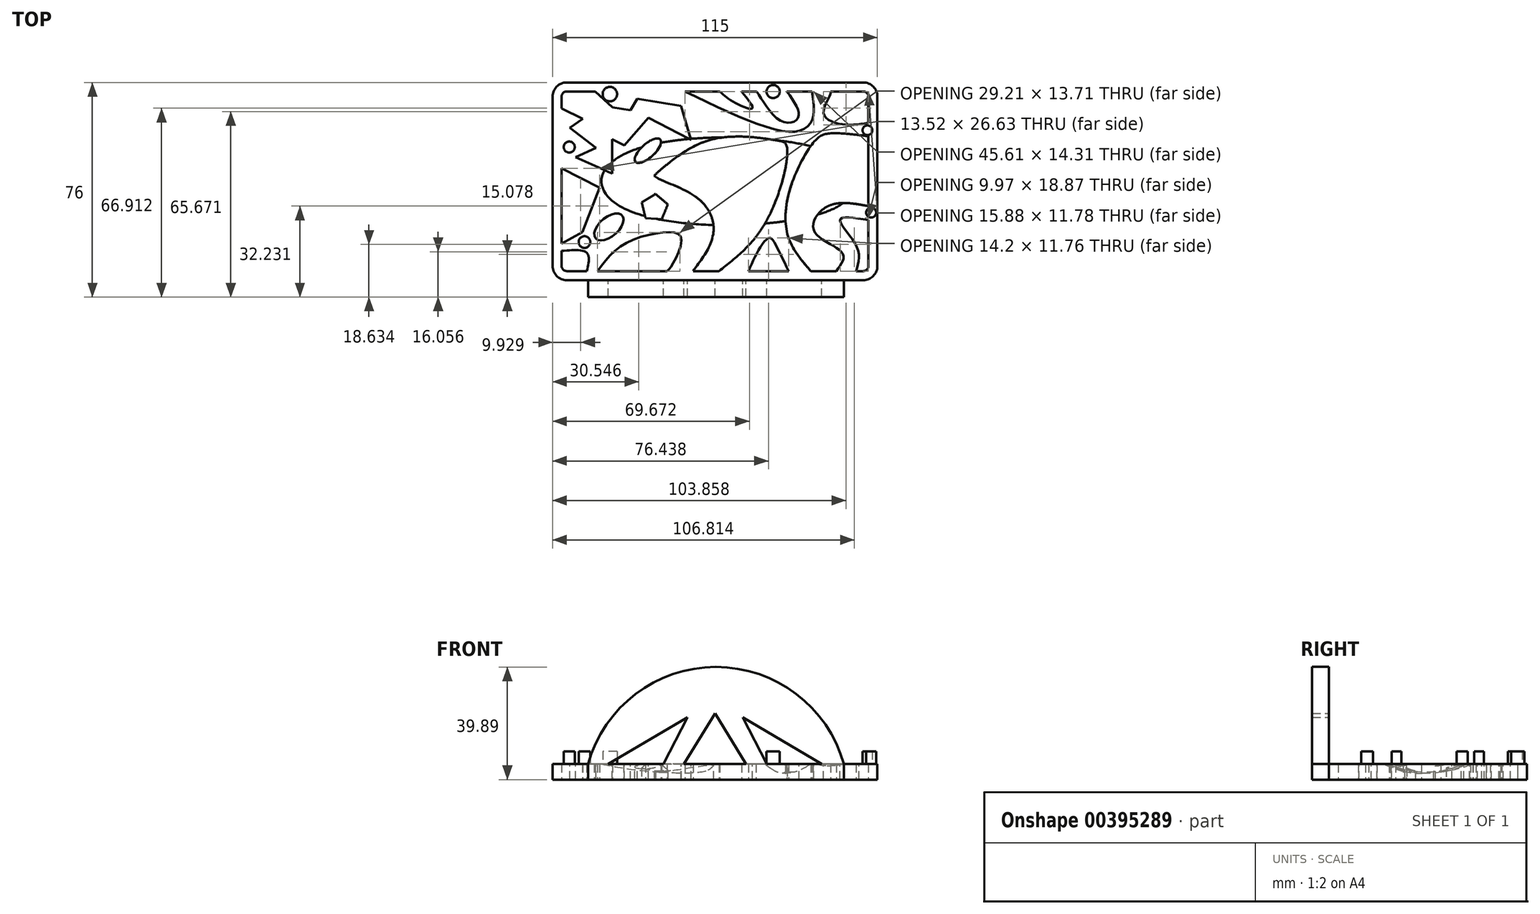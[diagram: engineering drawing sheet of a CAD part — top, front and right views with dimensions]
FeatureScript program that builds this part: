
annotation { "Feature Type Name" : "Feature", "Feature Type Description" : "" }
export const myFeature = defineFeature(function(context is Context, id is Id, definition is map)
    precondition{}
    {
        {
            var Q0;
            Q0=qCreatedBy(makeId("Top.planeOp"),FACE);
            var sketch = newSketch(context, id + "F0", { "sketchPlane" : qUnion([Q0])});
            skLineSegment(sketch, "E0.bottom", {"start": v(0, 0) * mm, "end": v(115, 0) * mm});
            skLineSegment(sketch, "E0.top", {"start": v(0, 70) * mm, "end": v(115, 70) * mm});
            skLineSegment(sketch, "E0.left", {"start": v(0, 0) * mm, "end": v(0, 70) * mm});
            skLineSegment(sketch, "E0.right", {"start": v(115, 0) * mm, "end": v(115, 70) * mm});
            skSolve(sketch);
        }
        {
            var Q0;
            Q0 = qSketchRegion(id + "F0", true);
            extrude(context, id + "F1", {"entities" : qUnion([Q0]), "depth" : 5.5 * mm});
        }
        {
            var Q0;
            Q0=makeQuery(id+"F1.opExtrude","SWEPT_EDGE",EDGE,{"disambiguationData":[OSD([sQuery(id+"F0.wireOp",EDGE,"E0.bottom"),sQuery(id+"F0.wireOp",EDGE,"E0.right")])]});
            var Q1;
            Q1=makeQuery(id+"F1.opExtrude","SWEPT_EDGE",EDGE,{"disambiguationData":[OSD([sQuery(id+"F0.wireOp",EDGE,"E0.top"),sQuery(id+"F0.wireOp",EDGE,"E0.right")])]});
            var Q2;
            Q2=makeQuery(id+"F1.opExtrude","SWEPT_EDGE",EDGE,{"disambiguationData":[OSD([sQuery(id+"F0.wireOp",EDGE,"E0.bottom"),sQuery(id+"F0.wireOp",EDGE,"E0.left")])]});
            var Q3;
            Q3=makeQuery(id+"F1.opExtrude","SWEPT_EDGE",EDGE,{"disambiguationData":[OSD([sQuery(id+"F0.wireOp",EDGE,"E0.top"),sQuery(id+"F0.wireOp",EDGE,"E0.left")])]});
            fillet(context, id + "F2", {"entities" : qUnion([Q0, Q1, Q2, Q3]), "radius" : 5 * mm, "tangentPropagation" : true, "allowEdgeOverflow" : false});
        }
        {
            var Q0;
            Q0=makeQuery(id+"F1.opExtrude","CAP_FACE",FACE,{"disambiguationData":[OSD([sQuery(id+"F0.wireOp",EDGE,"E0.bottom"),sQuery(id+"F0.wireOp",EDGE,"E0.top"),sQuery(id+"F0.wireOp",EDGE,"E0.left"),sQuery(id+"F0.wireOp",EDGE,"E0.right")])],"isStart":false});
            var sketch = newSketch(context, id + "F3", { "sketchPlane" : qUnion([Q0])});
            skArc(sketch, "E1.0", {"start": v(111.8, 65) * mm, "mid": v(111.27, 66.27) * mm, "end": v(110, 66.8) * mm});
            skLineSegment(sketch, "E1.1", {"start": v(111.8, 5) * mm, "end": v(111.8, 65) * mm});
            skLineSegment(sketch, "E1.2", {"start": v(110, 66.8) * mm, "end": v(5, 66.8) * mm});
            skArc(sketch, "E1.3", {"start": v(110, 3.2) * mm, "mid": v(111.27, 3.73) * mm, "end": v(111.8, 5) * mm});
            skArc(sketch, "E1.4", {"start": v(5, 66.8) * mm, "mid": v(3.73, 66.27) * mm, "end": v(3.2, 65) * mm});
            skLineSegment(sketch, "E1.5", {"start": v(3.2, 65) * mm, "end": v(3.2, 5) * mm});
            skArc(sketch, "E1.6", {"start": v(3.2, 5) * mm, "mid": v(3.73, 3.73) * mm, "end": v(5, 3.2) * mm});
            skLineSegment(sketch, "E1.7", {"start": v(5, 3.2) * mm, "end": v(110, 3.2) * mm});
            skSolve(sketch);
        }
        {
            var Q0;
            Q0=makeQuery(id+"F1.opExtrude","CAP_EDGE",EDGE,{"disambiguationData":[OSD([sQuery(id+"F0.wireOp",EDGE,"E0.right")])],"isStart":false});
            cPoint(context, id + "F4", {"entities" : qUnion([Q0]), "parameter" : 0.5});
        }
        {
            var Q0;
            Q0 = qCreatedBy(id + "F4" ,VERTEX);
            var Q1;
            Q1=qCreatedBy(makeId("Front.planeOp"),FACE);
            cPlane(context, id + "F5", {"entities" : qUnion([Q0, Q1]), "cplaneType" : CPlaneType.PLANE_POINT, "offset" : 25 * mm, "width" : 150 * mm, "height" : 150 * mm});
        }
        {
            var Q0;
            Q0=qCreatedBy(makeId("Top.planeOp"),FACE);
            var sketch = newSketch(context, id + "F6", { "sketchPlane" : qUnion([Q0])});
            skArc(sketch, "E2.0.0", {"start": v(3.2, 5) * mm, "mid": v(3.73, 3.73) * mm, "end": v(5, 3.2) * mm});
            skLineSegment(sketch, "E2.0.1", {"start": v(5, 3.2) * mm, "end": v(12.1, 3.2) * mm});
            skArc(sketch, "E2.0.2", {"start": v(110, 3.2) * mm, "mid": v(111.27, 3.73) * mm, "end": v(111.8, 5) * mm});
            skLineSegment(sketch, "E2.0.3", {"start": v(111.8, 5) * mm, "end": v(111.8, 21.3) * mm});
            skArc(sketch, "E2.0.4", {"start": v(111.8, 65) * mm, "mid": v(111.27, 66.27) * mm, "end": v(110, 66.8) * mm});
            skLineSegment(sketch, "E2.0.5", {"start": v(110, 66.8) * mm, "end": v(98.46, 66.8) * mm});
            skArc(sketch, "E2.0.6", {"start": v(5, 66.8) * mm, "mid": v(3.73, 66.27) * mm, "end": v(3.2, 65) * mm});
            skFitSpline(sketch, "E3", {"points": [v(111.8, 55.67) * mm, v(102.15, 55.24) * mm, v(95.98, 58.91) * mm, v(97.93, 64.83) * mm, v(98.46, 66.8) * mm], "startDerivative": vector(-29.87, -4.51) * mm, "endDerivative": vector(1.38, 11.14) * mm});
            skFitSpline(sketch, "E4", {"points": [v(111.8, 50.96) * mm, v(98.46, 52) * mm, v(93.18, 49.66) * mm, v(84.12, 32.4) * mm, v(83.54, 14.98) * mm, v(91.4, 3.2) * mm], "startDerivative": vector(-75.79, 9.38) * mm, "endDerivative": vector(46.5, -53.55) * mm});
            skFitSpline(sketch, "E5", {"points": [v(91.8, 66.8) * mm, v(92.04, 57.15) * mm, v(85.7, 52.56) * mm, v(46.87, 66.8) * mm], "startDerivative": vector(6.97, -41.3) * mm, "endDerivative": vector(-88.82, 42.95) * mm});
            skFitSpline(sketch, "E6", {"points": [v(58.9, 3.2) * mm, v(76.03, 21.56) * mm, v(82.86, 47.53) * mm, v(79.32, 49.48) * mm, v(54.72, 49.32) * mm, v(25.53, 27.54) * mm, v(3.2, 12.92) * mm], "startDerivative": vector(105.84, 82.15) * mm, "endDerivative": vector(-121.36, -67.42) * mm});
            skFitSpline(sketch, "E7", {"points": [v(83, 66.8) * mm, v(87.02, 57.68) * mm, v(80.58, 56.52) * mm, v(72.15, 66.8) * mm, v(72.02, 66.8) * mm], "startDerivative": vector(22.7, -31.9) * mm, "endDerivative": vector(-2.7, -1.87) * mm});
            skFitSpline(sketch, "E8", {"points": [v(66.9, 66.8) * mm, v(70.67, 60.83) * mm, v(64.36, 62.9) * mm, v(59.21, 66.8) * mm], "startDerivative": vector(19.38, -23.5) * mm, "endDerivative": vector(-12.93, 11.89) * mm});
            skFitSpline(sketch, "E9", {"points": [v(100.4, 3.2) * mm, v(102.64, 9.53) * mm, v(92.64, 17.27) * mm, v(97.1, 25.99) * mm, v(111.8, 26.2) * mm], "startDerivative": vector(25.53, 33.88) * mm, "endDerivative": vector(54.26, -10.38) * mm});
            skFitSpline(sketch, "E10", {"points": [v(83.54, 3.2) * mm, v(78.74, 12.92) * mm, v(76.9, 14.98) * mm, v(73.45, 11.57) * mm, v(69.34, 3.2) * mm], "startDerivative": vector(-16.54, 34.13) * mm, "endDerivative": vector(-12.58, -29.43) * mm});
            skFitSpline(sketch, "E11", {"points": [v(37.11, 66.8) * mm, v(56.97, 56.94) * mm, v(51.48, 53.5) * mm, v(27.34, 54.05) * mm, v(18.95, 40.98) * mm, v(3.2, 44.12) * mm], "startDerivative": vector(123.14, -43.65) * mm, "endDerivative": vector(-93.2, 43.1) * mm});
            skFitSpline(sketch, "E12", {"points": [v(49.73, 3.2) * mm, v(56.9, 16.67) * mm, v(52, 28.48) * mm, v(38.58, 35.4) * mm, v(35.9, 36.97) * mm], "startDerivative": vector(33.19, 44.6) * mm, "endDerivative": vector(-14.67, 10.37) * mm});
            skFitSpline(sketch, "E13", {"points": [v(15.94, 3.2) * mm, v(25.57, 12.92) * mm, v(41.21, 16.94) * mm, v(45.54, 14.98) * mm, v(42.48, 5.61) * mm, v(40.54, 3.2) * mm], "startDerivative": vector(31.9, 43.47) * mm, "endDerivative": vector(-14.4, -13.89) * mm});
            skLineSegment(sketch, "E14.trimOffspring", {"start": v(111.8, 55.67) * mm, "end": v(111.8, 65) * mm});
            skLineSegment(sketch, "E15.trimOffspring", {"start": v(91.8, 66.8) * mm, "end": v(83, 66.8) * mm});
            skLineSegment(sketch, "E16.trimOffspring", {"start": v(91.4, 3.2) * mm, "end": v(100.4, 3.2) * mm});
            skLineSegment(sketch, "E17.trimOffspring", {"start": v(69.34, 3.2) * mm, "end": v(83.54, 3.2) * mm});
            skLineSegment(sketch, "E18.trimOffspring", {"start": v(15.06, 66.8) * mm, "end": v(5, 66.8) * mm});
            skLineSegment(sketch, "E19.trimOffspring", {"start": v(3.2, 10.36) * mm, "end": v(3.2, 5) * mm});
            skLineSegment(sketch, "E20.trimOffspring", {"start": v(49.73, 3.2) * mm, "end": v(58.9, 3.2) * mm});
            skFitSpline(sketch, "E21", {"points": [v(12.1, 3.2) * mm, v(12.24, 9.54) * mm, v(3.2, 10.36) * mm], "startDerivative": vector(4.16, 16.75) * mm, "endDerivative": vector(-21.2, -1.88) * mm});
            skLineSegment(sketch, "E22.trimOffspring", {"start": v(72.15, 66.8) * mm, "end": v(66.9, 66.8) * mm});
            skLineSegment(sketch, "E23.trimOffspring", {"start": v(59.21, 66.8) * mm, "end": v(46.87, 66.8) * mm});
            skPoint(sketch, "E24.1.internal.orphan", {"position": v(20.32, 14.98) * mm});
            skFitSpline(sketch, "E25", {"points": [v(111.8, 21.3) * mm, v(101.78, 21.31) * mm, v(107.6, 12) * mm, v(107.5, 3.2) * mm], "startDerivative": vector(-43.28, 6.91) * mm, "endDerivative": vector(-7.66, -26.7) * mm});
            skLineSegment(sketch, "E26.trimOffspring", {"start": v(111.8, 26.2) * mm, "end": v(111.8, 50.96) * mm});
            skLineSegment(sketch, "E27.trimOffspring", {"start": v(107.5, 3.2) * mm, "end": v(110, 3.2) * mm});
            skLineSegment(sketch, "E28.trimOffspring", {"start": v(15.94, 3.2) * mm, "end": v(40.54, 3.2) * mm});
            skCircle(sketch, "E29.cCircle", {"center": v(36.07, 25.67) * mm, "radius": 3.94 * mm, "construction": true});
            skLineSegment(sketch, "E29.0", {"start": v(31.56, 27.53) * mm, "end": v(36.44, 30.53) * mm});
            skLineSegment(sketch, "E29.1", {"start": v(36.44, 30.53) * mm, "end": v(40.8, 26.81) * mm});
            skLineSegment(sketch, "E29.2", {"start": v(40.8, 26.81) * mm, "end": v(38.62, 21.52) * mm});
            skLineSegment(sketch, "E29.3", {"start": v(38.62, 21.52) * mm, "end": v(32.9, 21.96) * mm});
            skLineSegment(sketch, "E29.4", {"start": v(32.9, 21.96) * mm, "end": v(31.56, 27.53) * mm});
            skPoint(sketch, "E29.0.midPoint", {"position": v(34, 29.03) * mm});
            skEllipse(sketch, "E30", {"center": v(33.73, 45.83) * mm, "majorRadius": 5.9 * mm, "minorRadius": 2.4 * mm, "majorAxis": v(-0.74, -0.67)});
            skEllipse(sketch, "E31", {"center": v(19.93, 18.83) * mm, "majorRadius": 6.17 * mm, "minorRadius": 3.37 * mm, "majorAxis": v(-0.76, -0.65)});
            skFitSpline(sketch, "E32", {"points": [v(71.59, 14.86) * mm, v(68.14, 19.66) * mm, v(57, 18.22) * mm], "startDerivative": vector(-5.75, 14.27) * mm, "endDerivative": vector(-22.4, -6.52) * mm});
            skFitSpline(sketch, "E33", {"points": [v(77.17, 23.82) * mm, v(67.07, 25.78) * mm, v(68, 32.63) * mm, v(82.51, 40.16) * mm], "startDerivative": vector(-39.17, -0.09) * mm, "endDerivative": vector(43.07, 14.7) * mm});
            skFitSpline(sketch, "E34", {"points": [v(72.56, 50.45) * mm, v(68.9, 38.8) * mm, v(60.48, 34.86) * mm, v(59.2, 38.02) * mm, v(59.15, 50.35) * mm], "startDerivative": vector(-4.44, -43.64) * mm, "endDerivative": vector(0.5, 46.95) * mm});
            skFitSpline(sketch, "E35", {"points": [v(54.28, 26.06) * mm, v(55.75, 32.74) * mm, v(50.11, 40.64) * mm, v(41.76, 41.96) * mm], "startDerivative": vector(9.26, 20.94) * mm, "endDerivative": vector(-25.72, -0.75) * mm});
            skFitSpline(sketch, "E36.trimOffspring", {"points": [v(49.73, 3.2) * mm, v(56.9, 16.67) * mm, v(52, 28.48) * mm, v(38.58, 35.4) * mm, v(35.9, 36.97) * mm], "startDerivative": vector(33.19, 44.6) * mm, "endDerivative": vector(-14.67, 10.37) * mm});
            skLineSegment(sketch, "E37", {"start": v(83.1, 44.85) * mm, "end": v(78.59, 44.85) * mm});
            skLineSegment(sketch, "E38", {"start": v(78.59, 44.85) * mm, "end": v(77.4, 49.78) * mm});
            skLineSegment(sketch, "E39", {"start": v(3.17, 39.55) * mm, "end": v(16.69, 32.77) * mm});
            skLineSegment(sketch, "E40", {"start": v(16.69, 32.77) * mm, "end": v(10.57, 17.01) * mm});
            skLineSegment(sketch, "E41", {"start": v(3.2, 12.92) * mm, "end": v(3.17, 39.55) * mm});
            skLineSegment(sketch, "E42", {"start": v(3.2, 12.92) * mm, "end": v(10.57, 17.01) * mm});
            skLineSegment(sketch, "E43", {"start": v(28.52, 54.62) * mm, "end": v(15.06, 66.8) * mm});
            skLineSegment(sketch, "E44", {"start": v(24.23, 50.6) * mm, "end": v(3.2, 60.77) * mm});
            skLineSegment(sketch, "E45", {"start": v(3.2, 60.77) * mm, "end": v(3.2, 65) * mm});
            skLineSegment(sketch, "E46", {"start": v(97.1, 25.99) * mm, "end": v(90.65, 46.43) * mm});
            skLineSegment(sketch, "E47", {"start": v(100.7, 27.15) * mm, "end": v(102.26, 51.96) * mm});
            skSolve(sketch);
        }
        {
            var Q0;
            Q0 = qSketchRegion(id + "F6", true);
            extrude(context, id + "F7", {"entities" : qUnion([Q0]), "operationType" : NewBodyOperationType.REMOVE, "depth" : 25 * mm});
        }
        {
            var Q0;
            Q0=makeQuery(id+"F3.imprint","IMPRINT",FACE,{"disambiguationData":[TD([[makeQuery(id+"F3.imprint","IMPRINT",EDGE,{"derivedFrom":sQuery(id+"F3.wireOp",EDGE,"E1.0")}),1.0]])]});
            var sketch = newSketch(context, id + "F8", { "sketchPlane" : qUnion([Q0])});
            skLineSegment(sketch, "E48", {"start": v(48.99, 49.7) * mm, "end": v(45.5, 61.7) * mm});
            skLineSegment(sketch, "E49", {"start": v(45.5, 61.7) * mm, "end": v(30.03, 64.21) * mm});
            skLineSegment(sketch, "E50", {"start": v(30.03, 64.21) * mm, "end": v(27.51, 60.15) * mm});
            skLineSegment(sketch, "E51", {"start": v(27.51, 60.15) * mm, "end": v(6.82, 63.63) * mm});
            skLineSegment(sketch, "E52", {"start": v(6.82, 63.63) * mm, "end": v(11.07, 57.44) * mm});
            skLineSegment(sketch, "E53", {"start": v(11.07, 57.44) * mm, "end": v(6.06, 54) * mm});
            skLineSegment(sketch, "E54", {"start": v(6.06, 54) * mm, "end": v(15.33, 46.8) * mm});
            skLineSegment(sketch, "E55", {"start": v(15.33, 46.8) * mm, "end": v(8.17, 43.51) * mm});
            skLineSegment(sketch, "E56", {"start": v(8.17, 43.51) * mm, "end": v(21.13, 37.7) * mm});
            skLineSegment(sketch, "E57", {"start": v(21.13, 37.7) * mm, "end": v(21.13, 49.9) * mm});
            skLineSegment(sketch, "E58", {"start": v(21.13, 49.9) * mm, "end": v(25.39, 47.77) * mm});
            skLineSegment(sketch, "E59", {"start": v(25.39, 47.77) * mm, "end": v(33.9, 57.44) * mm});
            skLineSegment(sketch, "E60", {"start": v(33.9, 57.44) * mm, "end": v(48.99, 49.7) * mm});
            skSolve(sketch);
        }
        {
            var Q0;
            Q0 = qSketchRegion(id + "F8", true);
            extrude(context, id + "F9", {"entities" : qUnion([Q0]), "operationType" : NewBodyOperationType.REMOVE, "oppositeDirection" : true, "depth" : 25 * mm});
        }
        {
            var Q0;
            Q0=qCreatedBy(id+"F5.planeOp",FACE);
            var sketch = newSketch(context, id + "F10", { "sketchPlane" : qUnion([Q0])});
            skLineSegment(sketch, "E61", {"start": v(138.18, 36.2) * mm, "end": v(-8, 36.2) * mm});
            skFitSpline(sketch, "E62", {"points": [v(138.18, 36.2) * mm, v(114.3, 11) * mm, v(100.77, 4.2) * mm, v(3.46, 10.4) * mm, v(-8, 36.2) * mm], "startDerivative": vector(-127.6, -89.07) * mm, "endDerivative": vector(-40.31, 142.1) * mm});
            skSolve(sketch);
        }
        {
            var Q0;
            Q0 = qSketchRegion(id + "F10", true);
            var Q1;
            Q1=sQuery(id+"F10.wireOp",EDGE,"E61");
            revolve(context, id + "F11", {"operationType" : NewBodyOperationType.REMOVE, "entities" : qUnion([Q0]), "axis" : qUnion([Q1]), "revolveType" : RevolveType.FULL, "oppositeDirection" : true});
        }
        {
            var Q0;
            Q0=makeQuery(id+"F1.opExtrude","SWEPT_FACE",FACE,{"disambiguationData":[OSD([sQuery(id+"F0.wireOp",EDGE,"E0.bottom")])]});
            var sketch = newSketch(context, id + "F12", { "sketchPlane" : qUnion([Q0])});
            skArc(sketch, "E63", {"start": v(103.13, 5.5) * mm, "mid": v(57.83, 39.9) * mm, "end": v(12.53, 5.5) * mm});
            skLineSegment(sketch, "E64", {"start": v(57.5, 5.5) * mm, "end": v(57.5, 32.51) * mm, "construction": true});
            skPoint(sketch, "E64.endSnap0", {"position": v(57.5, 5.5) * mm});
            skLineSegment(sketch, "E65", {"start": v(46.49, 5.5) * mm, "end": v(57.5, 23.46) * mm});
            skLineSegment(sketch, "E66", {"start": v(39.21, 5.5) * mm, "end": v(47.7, 22.06) * mm});
            skLineSegment(sketch, "E67", {"start": v(47.7, 22.06) * mm, "end": v(19.71, 5.5) * mm});
            skLineSegment(sketch, "E68.MirrorCS", {"start": v(68.51, 5.5) * mm, "end": v(57.5, 23.46) * mm});
            skLineSegment(sketch, "E69.MirrorCS", {"start": v(67.3, 22.06) * mm, "end": v(95.29, 5.5) * mm});
            skLineSegment(sketch, "E70.MirrorCS", {"start": v(75.79, 5.5) * mm, "end": v(67.3, 22.06) * mm});
            skLineSegment(sketch, "E71", {"start": v(103.13, 5.5) * mm, "end": v(103.13, 0) * mm});
            skLineSegment(sketch, "E72", {"start": v(12.53, 5.5) * mm, "end": v(12.53, 0) * mm});
            skLineSegment(sketch, "E73", {"start": v(12.53, 0) * mm, "end": v(103.13, 0) * mm});
            skLineSegment(sketch, "E74", {"start": v(19.71, 5.5) * mm, "end": v(39.21, 5.5) * mm});
            skLineSegment(sketch, "E75", {"start": v(46.49, 5.5) * mm, "end": v(68.51, 5.5) * mm});
            skLineSegment(sketch, "E76", {"start": v(75.79, 5.5) * mm, "end": v(95.29, 5.5) * mm});
            skSolve(sketch);
        }
        {
            var Q0;
            Q0 = qSketchRegion(id + "F12", true);
            extrude(context, id + "F13", {"entities" : qUnion([Q0]), "operationType" : NewBodyOperationType.ADD, "depth" : 6 * mm});
        }
        {
            var Q0;
            Q0=qCreatedBy(makeId("Top.planeOp"),FACE);
            var sketch = newSketch(context, id + "F14", { "sketchPlane" : qUnion([Q0])});
            skCircle(sketch, "E77", {"center": v(20.28, 65.87) * mm, "radius": 2.55 * mm});
            skCircle(sketch, "E78", {"center": v(78.08, 66.79) * mm, "radius": 2.33 * mm});
            skCircle(sketch, "E79", {"center": v(112.78, 23.9) * mm, "radius": 1.76 * mm});
            skCircle(sketch, "E80", {"center": v(111.46, 53.07) * mm, "radius": 1.74 * mm});
            skCircle(sketch, "E81", {"center": v(5.9, 47.13) * mm, "radius": 1.96 * mm});
            skCircle(sketch, "E82", {"center": v(11.3, 13.48) * mm, "radius": 2.06 * mm});
            skSolve(sketch);
        }
        {
            var Q0;
            Q0 = qSketchRegion(id + "F14", true);
            extrude(context, id + "F15", {"entities" : qUnion([Q0]), "operationType" : NewBodyOperationType.ADD, "depth" : 10 * mm});
        }
    });
